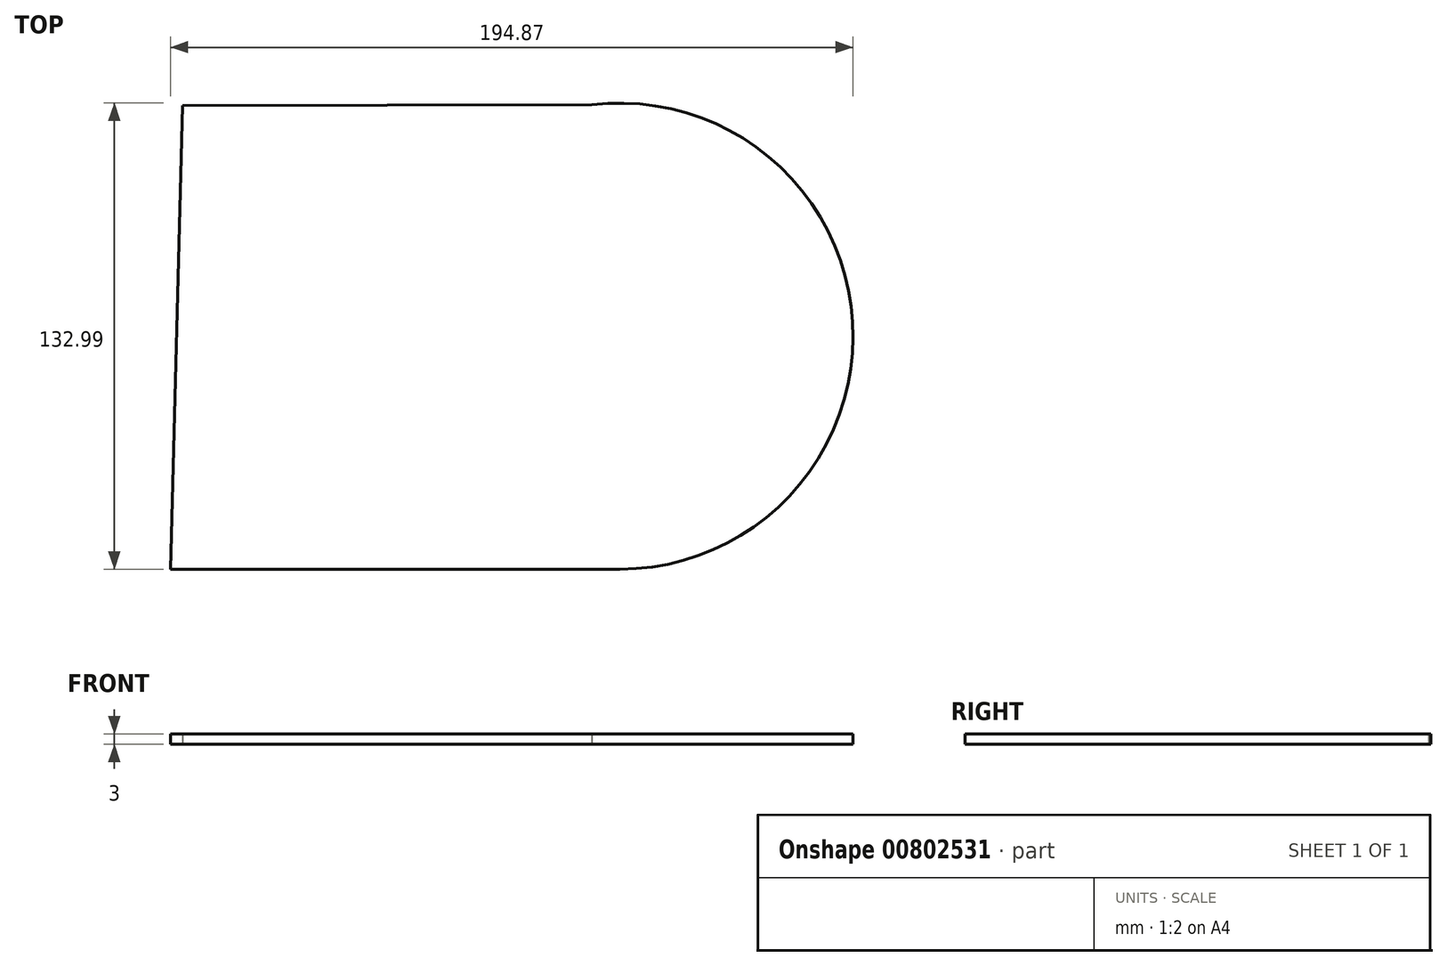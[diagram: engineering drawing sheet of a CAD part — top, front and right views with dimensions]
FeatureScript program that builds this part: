
annotation { "Feature Type Name" : "Feature", "Feature Type Description" : "" }
export const myFeature = defineFeature(function(context is Context, id is Id, definition is map)
    precondition{}
    {
        {
            var Q0;
            Q0=qCreatedBy(makeId("Top.planeOp"),FACE);
            var sketch = newSketch(context, id + "F0", { "sketchPlane" : qUnion([Q0])});
            skArc(sketch, "E0", {"start": v(0, -67.28) * mm, "mid": v(66.37, 3.27) * mm, "end": v(-8.1, 65.21) * mm});
            skLineSegment(sketch, "E1", {"start": v(-128.37, -67.28) * mm, "end": v(-124.93, 65.06) * mm});
            skLineSegment(sketch, "E2", {"start": v(-124.93, 65.06) * mm, "end": v(-8.1, 65.21) * mm});
            skLineSegment(sketch, "E3", {"start": v(-128.37, -67.28) * mm, "end": v(0, -67.28) * mm});
            skSolve(sketch);
        }
        {
            var Q0;
            Q0 = qSketchRegion(id + "F0", true);
            extrude(context, id + "F1", {"entities" : qUnion([Q0]), "depth" : 3 * mm, "offsetDistance" : 25 * mm});
        }
    });
